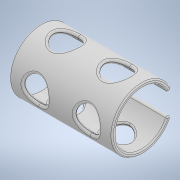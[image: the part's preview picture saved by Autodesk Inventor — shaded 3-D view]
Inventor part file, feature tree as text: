
AUTODESK INVENTOR PART (.ipt)
format: ipt  version: 2020 (Build 240168000, 168)  size: 511,488 bytes
history: native  units: in
note: dims shown in document units (in); Inventor stores cm internally (conversion verified against a paired STEP export)
features: extrude x3, fillet x3, sketch x3
ambient origin geometry x8: Origin, YZ Plane, XZ Plane, XY Plane, X Axis, Y Axis, Z Axis, Center Point
bodies: Solid1 (feature_tree)
feature tree (9):
  extrude  "Extrusion1"  Depth=0.0787in
  extrude  "Extrusion2"  Depth=0.0197in
  extrude  "Extrusion3"  Depth=0.0236in
  fillet  "Fillet1"  Radius=0.0197in
  fillet  "Fillet2"  Radius=0.0591in
  fillet  "Fillet3"  Radius=0.0591in
  sketch  "Sketch1"  dims[d0=1.1811in d1=0.0787in]
  sketch  "Sketch2"  dims[d2=0.481in d3=0.0197in]
  sketch  "Sketch3"  dims[d4=0.0197in d5=0.0197in d6=0.0197in d7=0.0591in d8=0.0591in d9=0.0591in d10=0.0591in d11=0.0591in d12=0.0591in d13=0.0197in d14=0.0197in d15=0.0197in d16=0.0197in d17=1.9685in d18=0.0in d19=0.4724in d20=0.4724in d21=1.9685in d22=0.0in d23=0.4724in d24=0.4724in d25=1.9685in d26=0.0in d27=0.0394in d28=0.0354in d29=0.0236in]
